# Revit family: MINIMAL_2000MM
name_source: partatom
category: Lighting Fixtures
units: mm (PartAtom-declared; Revit-internal decimal feet)

## family parameters
Always vertical = Yes
Cut with Voids When Loaded = No
Host = Ceiling
Light Source = Yes
OmniClass Number = 23.80.70.11
OmniClass Title = Luminaries for Internal Lighting
Part Type = Normal
Room Calculation Point = No
Round Connector Dimension = Use Diameter
Shared = No

## types (1)
- MINIMAL_2000MM
    Color Filter = 16777215
    Default Elevation = 0 mm  [stored 0 ft]
    Dimensions = 15x3 mm, L : 2000 mm
    Dimming Lamp Color Temperature Shift = <None>
    Driver = Driver externe
    Emit from Line Length = 609.6 mm  [stored 2 ft]
    Fintion = Gris aluminium
    Light Source Symbol Size = 609.6 mm  [stored 2 ft]
    Matériau = Aluminium
    Type = Barette aluminium
    Type de lampe = Ruban LED

note: [stored X ft] marks values corroborated as IEEE doubles in the binary element streams (Revit-internal decimal feet)

## geometry (parser evidence)
native form markers: Sweep x3
no freeform markers — native parametric forms only
